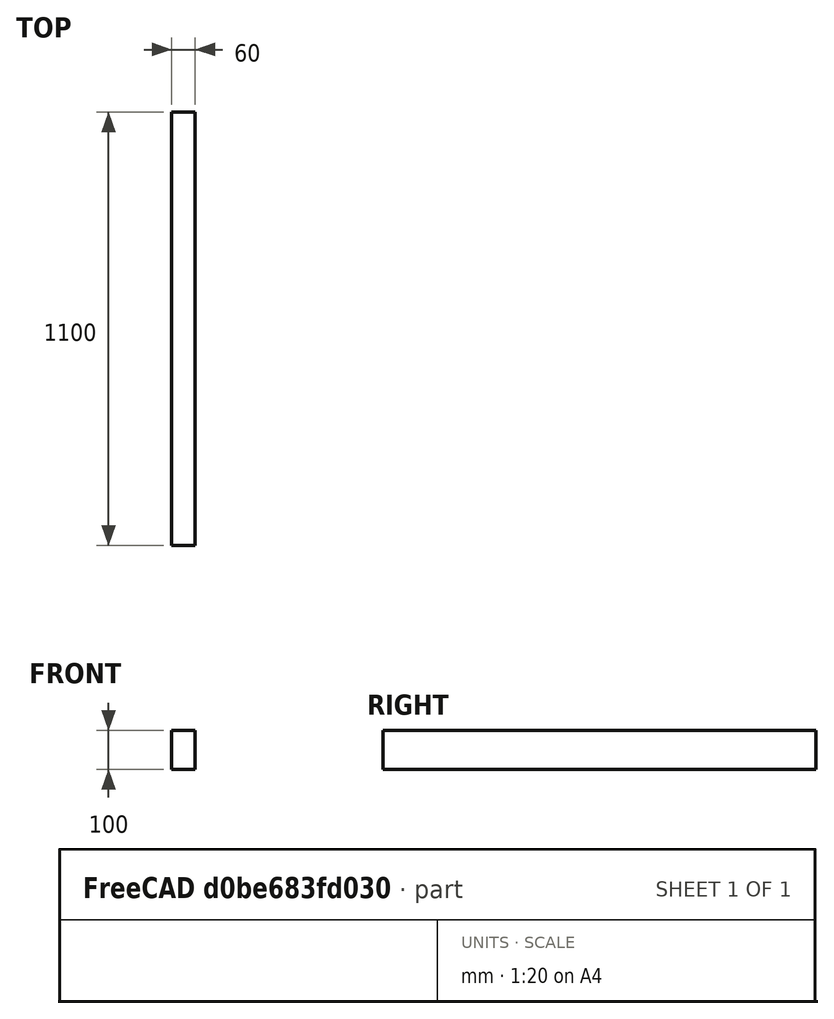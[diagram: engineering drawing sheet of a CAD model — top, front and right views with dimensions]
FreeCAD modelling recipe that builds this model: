
FCSTD DOCUMENT  (FreeCAD 1.0RUnknown)
Label: beam60x100x1100
License: All rights reserved
LicenseURL: https://en.wikipedia.org/wiki/All_rights_reserved
objects: PartDesign::CoordinateSystem×3, Sketcher::SketchObject×1, PartDesign::Pad×1, PartDesign::Body×1, App::Part×1
note: 9 computed .brp shape members not serialized (recipe doc carries the construction recipe); baked Part::Feature solids carry a one-line shape summary decoded from their .brp

FEATURE [Sketcher::SketchObject] Sketch
  ArcFitTolerance = 1e-06
  AttachmentSupport = -> [XZ_Plane]
  FullyConstrained = true
  MakeInternals = false
  MapMode = 5
  Placement = pos=(0,0,0) rot=(1,0,0;1.5708rad)
  sketch-geometry (5):
    g0: LineSegment StartX=-30 StartY=-50 StartZ=0 EndX=30 EndY=-50 EndZ=0
    g1: LineSegment StartX=30 StartY=-50 StartZ=0 EndX=30 EndY=50 EndZ=0
    g2: LineSegment StartX=30 StartY=50 StartZ=0 EndX=-30 EndY=50 EndZ=0
    g3: LineSegment StartX=-30 StartY=50 StartZ=0 EndX=-30 EndY=-50 EndZ=0
    g4: GeomPoint [constr] X=0 Y=0 Z=0
  constraints (12):
    c: Coincident(g0,g1)
    c: Coincident(g1,g2)
    c: Coincident(g2,g3)
    c: Coincident(g3,g0)
    c: Horizontal(g0)
    c: Horizontal(g2)
    c: Vertical(g1)
    c: Vertical(g3)
    c: Symmetric(g2,g0,g4)
    c: Coincident(g4,g-1)
    c: DistanceX(g0,g0) = 60
    c: DistanceY(g3,g3) = 100
FEATURE [PartDesign::Pad] Pad
  Direction = (0,-1,2e-16)
  Length = 1100
  Length2 = 10
  Midplane = true
  Placement = pos=(0,0,0) rot=(1,0,0;1.5708rad)
  Profile = -> Sketch
  ReferenceAxis = -> Sketch [N_Axis]
  Refine = true
  Suppressed = false
  Type = 0
FEATURE [PartDesign::Body] Body  label="Körper"
  AllowCompound = false
  Group = -> [Sketch,Pad]
  Origin = -> Origin
  Tip = -> Pad
FEATURE [PartDesign::CoordinateSystem] LCS_Origin
  AttacherType = Attacher::AttachEngine3D
  AttachmentSupport = -> [X_Axis001]
  MapMode = 2
FEATURE [PartDesign::CoordinateSystem] LCS_1
  AttacherType = Attacher::AttachEngine3D
  AttachmentSupport = -> [Pad]
  MapMode = 45
  Placement = pos=(-30,550,-2.44e-13) rot=(0,0,1;0rad)
FEATURE [PartDesign::CoordinateSystem] LCS_2
  AttacherType = Attacher::AttachEngine3D
  AttachmentSupport = -> [Pad]
  MapMode = 45
  Placement = pos=(-30,-550,2.44e-13) rot=(0,0,1;0rad)
FEATURE [App::Part] beam60x100x887  label="beam60x100x1100"
  Group = -> [LCS_Origin,Body,LCS_1,LCS_2]
  Origin = -> Origin001
